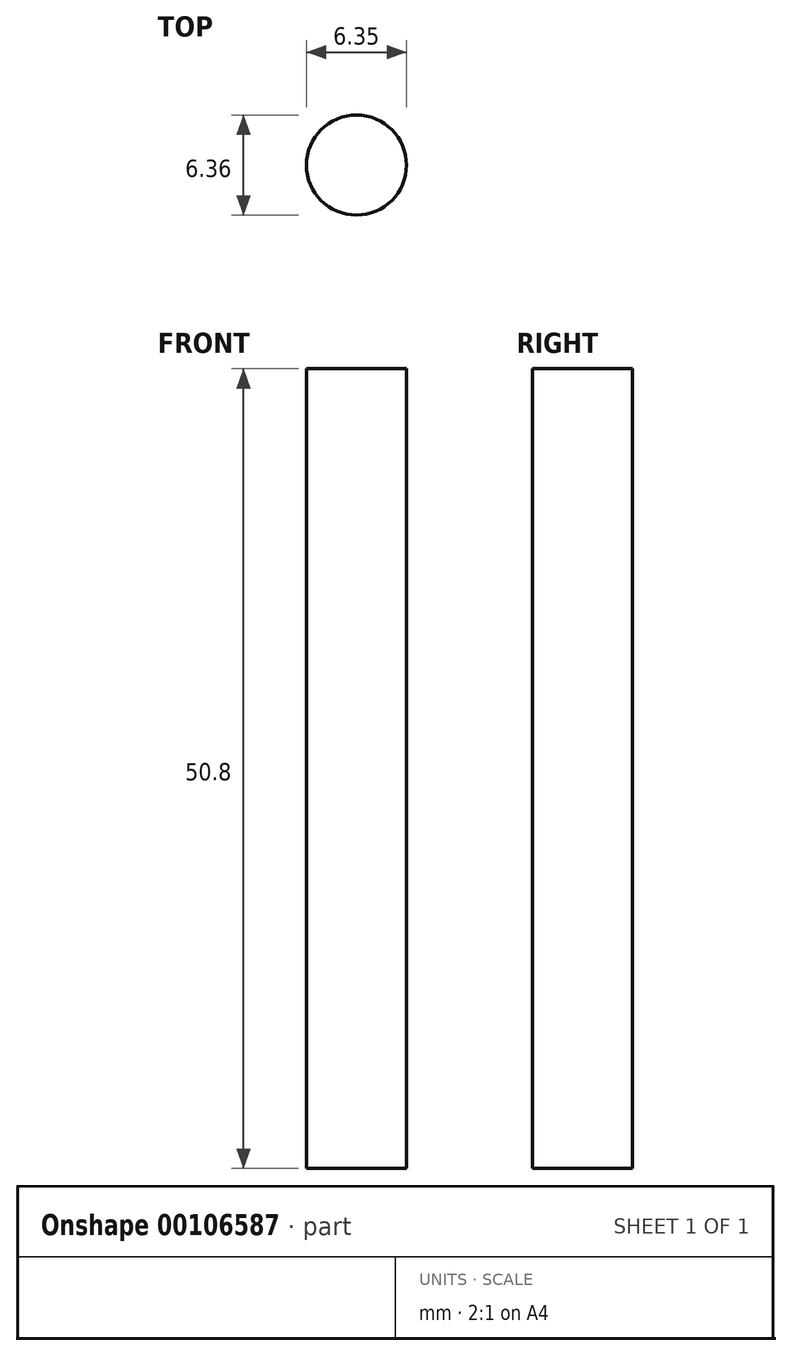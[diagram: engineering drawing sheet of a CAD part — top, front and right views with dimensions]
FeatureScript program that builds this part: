
annotation { "Feature Type Name" : "Feature", "Feature Type Description" : "" }
export const myFeature = defineFeature(function(context is Context, id is Id, definition is map)
    precondition{}
    {
        {
            var Q0;
            Q0=qCreatedBy(makeId("Front.planeOp"),FACE);
            var sketch = newSketch(context, id + "F0", { "sketchPlane" : qUnion([Q0])});
            skLineSegment(sketch, "E0.bottom", {"start": v(-30.7, 29.43) * mm, "end": v(-27.52, 29.43) * mm});
            skLineSegment(sketch, "E0.top", {"start": v(-30.7, -21.37) * mm, "end": v(-27.52, -21.37) * mm});
            skLineSegment(sketch, "E0.left", {"start": v(-30.7, 29.43) * mm, "end": v(-30.7, -21.37) * mm});
            skLineSegment(sketch, "E0.right", {"start": v(-27.52, 29.43) * mm, "end": v(-27.52, -21.37) * mm});
            skSolve(sketch);
        }
        {
            var Q0;
            Q0=makeQuery(id+"F0.imprint","IMPRINT",FACE,{"disambiguationData":[TD([[makeQuery(id+"F0.imprint","IMPRINT",EDGE,{"derivedFrom":sQuery(id+"F0.wireOp",EDGE,"E0.bottom")}),-1.0]])]});
            var Q1;
            Q1=sQuery(id+"F0.wireOp",EDGE,"E0.left");
            revolve(context, id + "F1", {"entities" : qUnion([Q0]), "axis" : qUnion([Q1]), "revolveType" : RevolveType.FULL});
        }
    });
